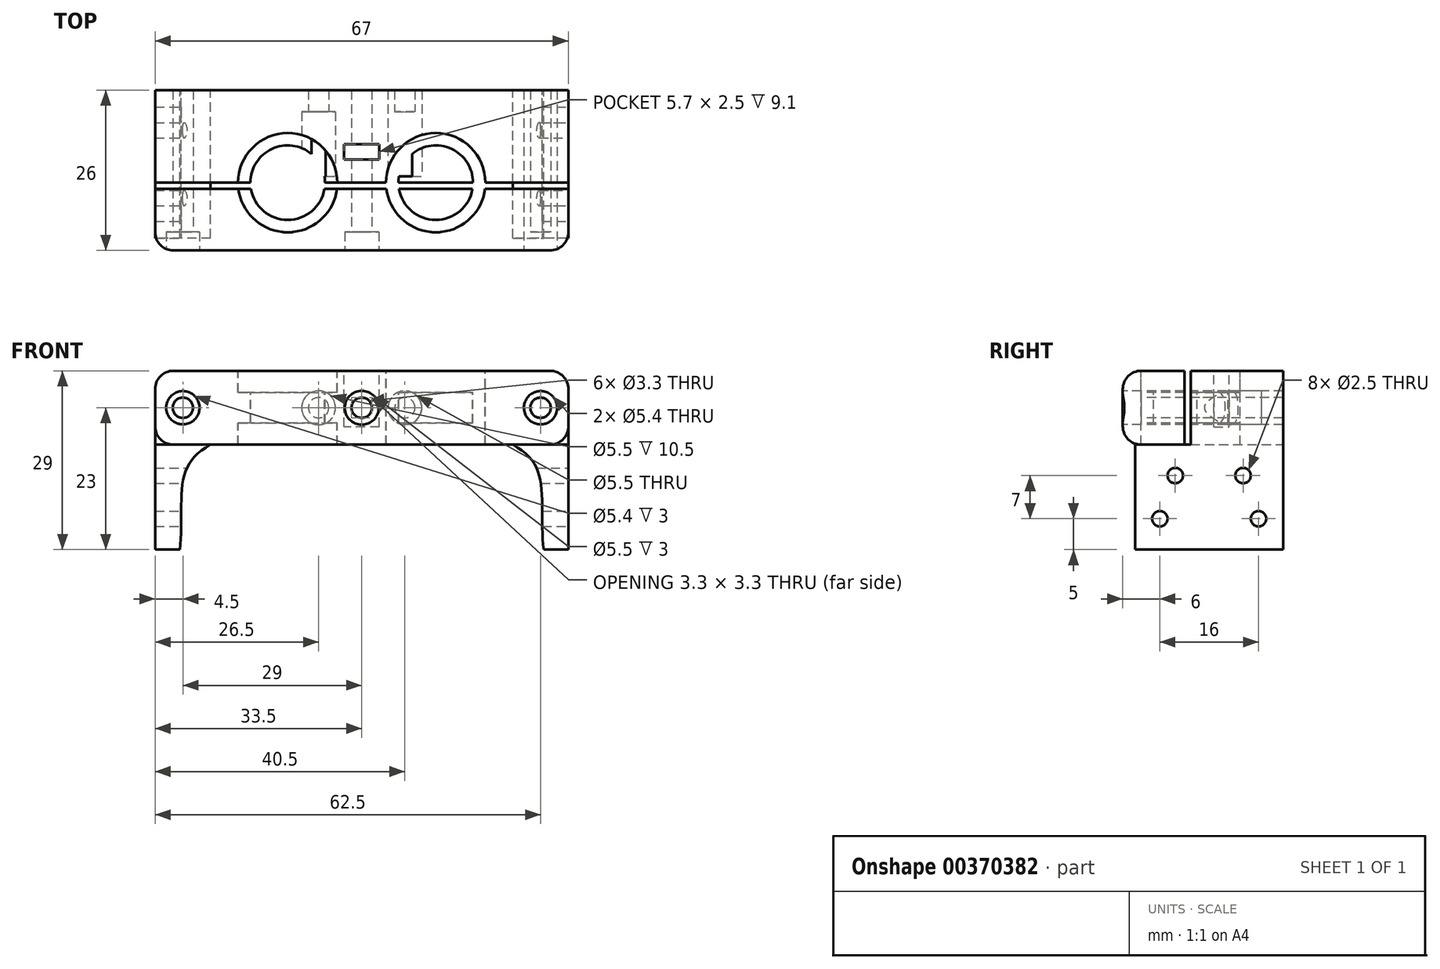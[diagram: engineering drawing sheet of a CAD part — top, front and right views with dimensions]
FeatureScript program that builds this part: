
annotation { "Feature Type Name" : "Feature", "Feature Type Description" : "" }
export const myFeature = defineFeature(function(context is Context, id is Id, definition is map)
    precondition{}
    {
        {
            var Q0;
            Q0=qCreatedBy(makeId("Front.planeOp"),FACE);
            var sketch = newSketch(context, id + "F0", { "sketchPlane" : qUnion([Q0])});
            skLineSegment(sketch, "E0.bottom", {"start": v(33.5, -6) * mm, "end": v(-33.5, -6) * mm});
            skLineSegment(sketch, "E0.top", {"start": v(33.5, 6) * mm, "end": v(-33.5, 6) * mm});
            skLineSegment(sketch, "E0.left", {"start": v(33.5, -6) * mm, "end": v(33.5, 6) * mm});
            skLineSegment(sketch, "E0.right", {"start": v(-33.5, -6) * mm, "end": v(-33.5, 6) * mm});
            skPoint(sketch, "E0.middle", {"position": v(0, 0) * mm});
            skLineSegment(sketch, "E1", {"start": v(-33.5, -23) * mm, "end": v(-33.5, -6) * mm});
            skLineSegment(sketch, "E2.MirrorCS", {"start": v(33.5, -23) * mm, "end": v(33.5, -6) * mm});
            skLineSegment(sketch, "E3", {"start": v(-33.5, -23) * mm, "end": v(-29.5, -23) * mm});
            skLineSegment(sketch, "E4.MirrorCS", {"start": v(33.5, -23) * mm, "end": v(29.5, -23) * mm});
            skFitSpline(sketch, "E5", {"points": [v(-24.5, -6) * mm, v(-29, -12) * mm, v(-29.5, -23) * mm], "startDerivative": vector(-19.18, -10.42) * mm, "endDerivative": vector(-2.52, -19.68) * mm});
            skFitSpline(sketch, "E6.MirrorCS", {"points": [v(24.5, -6) * mm, v(29, -12) * mm, v(29.5, -23) * mm], "startDerivative": vector(19.18, -10.42) * mm, "endDerivative": vector(2.52, -19.68) * mm});
            skSolve(sketch);
        }
        {
            var Q0;
            Q0=makeQuery(id+"F0.imprint","IMPRINT",FACE,{"disambiguationData":[TD([[makeQuery(id+"F0.imprint","IMPRINT",EDGE,{"derivedFrom":sQuery(id+"F0.wireOp",EDGE,"E0.top")}),1.0]])]});
            extrude(context, id + "F1", {"entities" : qUnion([Q0]), "depth" : 15 * mm, "offsetDistance" : 25 * mm});
        }
        {
            var Q0;
            {var subQ0=sQuery(id+"F0.wireOp",EDGE,"E1");Q0=makeQuery(id+"F0.imprint","IMPRINT",FACE,{"disambiguationData":[TD([[makeQuery(id+"F0.imprint","IMPRINT",EDGE,{"derivedFrom":subQ0}),-1.0]])]});}
            var Q1;
            {var subQ0=sQuery(id+"F0.wireOp",EDGE,"E2.MirrorCS");Q1=makeQuery(id+"F0.imprint","IMPRINT",FACE,{"disambiguationData":[TD([[makeQuery(id+"F0.imprint","IMPRINT",EDGE,{"derivedFrom":subQ0}),1.0]])]});}
            extrude(context, id + "F2", {"entities" : qUnion([Q0, Q1]), "operationType" : NewBodyOperationType.ADD, "depth" : 24 * mm, "offsetDistance" : 25 * mm});
        }
        {
            var Q0;
            Q0=makeQuery(id+"F1.opExtrude","SWEPT_FACE",FACE,{"disambiguationData":[OSD([sQuery(id+"F0.wireOp",EDGE,"E0.top")])]});
            var sketch = newSketch(context, id + "F3", { "sketchPlane" : qUnion([Q0])});
            skLineSegment(sketch, "E7", {"start": v(-33.5, -7) * mm, "end": v(33.5, -7) * mm, "construction": true});
            skLineSegment(sketch, "E8.bottom", {"start": v(2.85, -11.25) * mm, "end": v(-2.85, -11.25) * mm});
            skLineSegment(sketch, "E8.top", {"start": v(2.85, -8.75) * mm, "end": v(-2.85, -8.75) * mm});
            skLineSegment(sketch, "E8.left", {"start": v(2.85, -11.25) * mm, "end": v(2.85, -8.75) * mm});
            skLineSegment(sketch, "E8.right", {"start": v(-2.85, -11.25) * mm, "end": v(-2.85, -8.75) * mm});
            skPoint(sketch, "E8.middle", {"position": v(0, -10) * mm});
            skSolve(sketch);
        }
        {
            var Q0;
            Q0=makeQuery(id+"F3.imprint","IMPRINT",FACE,{"disambiguationData":[TD([[makeQuery(id+"F3.imprint","IMPRINT",EDGE,{"derivedFrom":sQuery(id+"F3.wireOp",EDGE,"jUf4XIvJ-XALh-Ccey-Qydy-tmJyOFJsBozL.bottom")}),-1.0]])]});
            var Q1;
            Q1=makeQuery(id+"F3.imprint","IMPRINT",FACE,{"disambiguationData":[TD([[makeQuery(id+"F3.imprint","IMPRINT",EDGE,{"derivedFrom":sQuery(id+"F3.wireOp",EDGE,"E8.bottom")}),-1.0]])]});
            var Q2;
            Q2=makeQuery(id+"F3.imprint","IMPRINT",FACE,{"disambiguationData":[TD([[makeQuery(id+"F3.imprint","IMPRINT",EDGE,{"derivedFrom":sQuery(id+"F3.wireOp",EDGE,"7975c7f9-c37b-4ea5-b004-56becf66a4950.MirrorCS")}),1.0]])]});
            extrude(context, id + "F4", {"entities" : qUnion([Q0, Q1, Q2]), "operationType" : NewBodyOperationType.REMOVE, "oppositeDirection" : true, "depth" : 9.1 * mm, "offsetDistance" : 25 * mm});
        }
        {
            var Q0;
            Q0=qCreatedBy(makeId("Top.planeOp"),FACE);
            var sketch = newSketch(context, id + "F5", { "sketchPlane" : qUnion([Q0])});
            skLineSegment(sketch, "E9.bottom", {"start": v(33.5, -26) * mm, "end": v(-33.5, -26) * mm});
            skLineSegment(sketch, "E9.top", {"start": v(33.5, -16) * mm, "end": v(-33.5, -16) * mm});
            skLineSegment(sketch, "E9.left", {"start": v(33.5, -26) * mm, "end": v(33.5, -16) * mm});
            skLineSegment(sketch, "E9.right", {"start": v(-33.5, -26) * mm, "end": v(-33.5, -16) * mm});
            skPoint(sketch, "E9.middle", {"position": v(0, -21) * mm});
            skSolve(sketch);
        }
        {
            var Q0;
            Q0=makeQuery(id+"F5.imprint","IMPRINT",FACE,{"disambiguationData":[TD([[makeQuery(id+"F5.imprint","IMPRINT",EDGE,{"derivedFrom":sQuery(id+"F5.wireOp",EDGE,"E9.bottom")}),-1.0]])]});
            extrude(context, id + "F6", {"entities" : qUnion([Q0]), "endBound" : BoundingType.SYMMETRIC, "depth" : 12 * mm, "offsetDistance" : 25 * mm});
        }
        {
            var Q0;
            Q0=makeQuery(id+"F6.opExtrude","SWEPT_FACE",FACE,{"disambiguationData":[OSD([sQuery(id+"F5.wireOp",EDGE,"E9.bottom")])]});
            var sketch = newSketch(context, id + "F7", { "sketchPlane" : qUnion([Q0])});
            skCircle(sketch, "E10", {"center": v(-7, 0) * mm, "radius": 1.65 * mm});
            skCircle(sketch, "E11.MirrorC", {"center": v(7, 0) * mm, "radius": 1.65 * mm});
            skCircle(sketch, "E12", {"center": v(-7, 0) * mm, "radius": 2.75 * mm});
            skCircle(sketch, "E13.MirrorC", {"center": v(7, 0) * mm, "radius": 2.75 * mm});
            skCircle(sketch, "E14", {"center": v(-29, 0) * mm, "radius": 1.65 * mm});
            skCircle(sketch, "E15", {"center": v(0, 0) * mm, "radius": 1.65 * mm});
            skCircle(sketch, "E16.MirrorC", {"center": v(29, 0) * mm, "radius": 1.65 * mm});
            skCircle(sketch, "E17", {"center": v(-29, 0) * mm, "radius": 2.7 * mm});
            skCircle(sketch, "E18", {"center": v(0, 0) * mm, "radius": 2.75 * mm});
            skCircle(sketch, "E19", {"center": v(29, 0) * mm, "radius": 2.7 * mm});
            skSolve(sketch);
        }
        {
            var Q0;
            Q0=makeQuery(id+"F7.imprint","IMPRINT",FACE,{"disambiguationData":[TD([[makeQuery(id+"F7.imprint","IMPRINT",EDGE,{"derivedFrom":sQuery(id+"F7.wireOp",EDGE,"E10")}),1.0]])]});
            var Q1;
            Q1=makeQuery(id+"F7.imprint","IMPRINT",FACE,{"disambiguationData":[TD([[makeQuery(id+"F7.imprint","IMPRINT",EDGE,{"derivedFrom":sQuery(id+"F7.wireOp",EDGE,"E11.MirrorC")}),-1.0]])]});
            extrude(context, id + "F8", {"entities" : qUnion([Q0, Q1]), "operationType" : NewBodyOperationType.REMOVE, "oppositeDirection" : true, "depth" : 30.5 * mm, "offsetDistance" : 25 * mm, "hasSecondDirection" : true, "secondDirectionOppositeDirection" : true, "secondDirectionDepth" : 12 * mm});
        }
        {
            var Q0;
            Q0=makeQuery(id+"F7.imprint","IMPRINT",FACE,{"disambiguationData":[TD([[makeQuery(id+"F7.imprint","IMPRINT",EDGE,{"derivedFrom":sQuery(id+"F7.wireOp",EDGE,"E10")}),-1.0]])]});
            var Q1;
            Q1=makeQuery(id+"F7.imprint","IMPRINT",FACE,{"disambiguationData":[TD([[makeQuery(id+"F7.imprint","IMPRINT",EDGE,{"derivedFrom":sQuery(id+"F7.wireOp",EDGE,"E11.MirrorC")}),1.0]])]});
            extrude(context, id + "F9", {"entities" : qUnion([Q0, Q1]), "operationType" : NewBodyOperationType.REMOVE, "oppositeDirection" : true, "depth" : 22.5 * mm, "offsetDistance" : 25 * mm, "hasSecondDirection" : true, "secondDirectionOppositeDirection" : true, "secondDirectionDepth" : 12 * mm});
        }
        {
            var Q0;
            Q0=makeQuery(id+"F7.imprint","IMPRINT",FACE,{"disambiguationData":[TD([[makeQuery(id+"F7.imprint","IMPRINT",EDGE,{"derivedFrom":sQuery(id+"F7.wireOp",EDGE,"E14")}),1.0]])]});
            var Q1;
            Q1=makeQuery(id+"F7.imprint","IMPRINT",FACE,{"disambiguationData":[TD([[makeQuery(id+"F7.imprint","IMPRINT",EDGE,{"derivedFrom":sQuery(id+"F7.wireOp",EDGE,"E15")}),1.0]])]});
            var Q2;
            Q2=makeQuery(id+"F7.imprint","IMPRINT",FACE,{"disambiguationData":[TD([[makeQuery(id+"F7.imprint","IMPRINT",EDGE,{"derivedFrom":sQuery(id+"F7.wireOp",EDGE,"E16.MirrorC")}),-1.0]])]});
            extrude(context, id + "F10", {"entities" : qUnion([Q0, Q1, Q2]), "operationType" : NewBodyOperationType.REMOVE, "oppositeDirection" : true, "depth" : 45 * mm, "offsetDistance" : 25 * mm});
        }
        {
            var Q0;
            Q0=makeQuery(id+"F1.opExtrude","SWEPT_FACE",FACE,{"disambiguationData":[OSD([sQuery(id+"F0.wireOp",EDGE,"E0.top")])]});
            var sketch = newSketch(context, id + "F11", { "sketchPlane" : qUnion([Q0])});
            skCircle(sketch, "E20", {"center": v(-12, -15) * mm, "radius": 8.05 * mm});
            skCircle(sketch, "E21", {"center": v(-12, -15) * mm, "radius": 6.05 * mm});
            skCircle(sketch, "E22.MirrorC", {"center": v(12, -15) * mm, "radius": 6.05 * mm});
            skCircle(sketch, "E23.MirrorC", {"center": v(12, -15) * mm, "radius": 8.05 * mm});
            skSolve(sketch);
        }
        {
            var Q0;
            {var subQ0=sQuery(id+"F11.wireOp",EDGE,"E21");var subQ1=makeQuery(id+"F1.opExtrude","CAP_EDGE",EDGE,{"disambiguationData":[OSD([sQuery(id+"F0.wireOp",EDGE,"E0.top")])],"isStart":false});var subQ2=makeQuery(id+"F11.imprint","INTERSECT",VERTEX,{"disambiguationData":[OD(0.0)],"derivedFrom":[subQ1,subQ0]});Q0=makeQuery(id+"F11.imprint","IMPRINT",FACE,{"disambiguationData":[TD([[makeQuery(id+"F11.imprint","IMPRINT",EDGE,{"disambiguationData":[TD([[subQ2,1.0]])],"derivedFrom":subQ0}),1.0]])]});}
            var Q1;
            {var subQ0=sQuery(id+"F11.wireOp",EDGE,"E22.MirrorC");var subQ1=makeQuery(id+"F1.opExtrude","CAP_EDGE",EDGE,{"disambiguationData":[OSD([sQuery(id+"F0.wireOp",EDGE,"E0.top")])],"isStart":false});var subQ2=makeQuery(id+"F11.imprint","INTERSECT",VERTEX,{"disambiguationData":[OD(0.0)],"derivedFrom":[subQ1,subQ0]});Q1=makeQuery(id+"F11.imprint","IMPRINT",FACE,{"disambiguationData":[TD([[makeQuery(id+"F11.imprint","IMPRINT",EDGE,{"disambiguationData":[TD([[subQ2,1.0]])],"derivedFrom":subQ0}),-1.0]])]});}
            var Q2;
            {var subQ0=sQuery(id+"F11.wireOp",EDGE,"E21");var subQ1=makeQuery(id+"F1.opExtrude","CAP_EDGE",EDGE,{"disambiguationData":[OSD([sQuery(id+"F0.wireOp",EDGE,"E0.top")])],"isStart":false});var subQ2=makeQuery(id+"F11.imprint","INTERSECT",VERTEX,{"disambiguationData":[OD(0.0)],"derivedFrom":[subQ1,subQ0]});Q2=makeQuery(id+"F11.imprint","IMPRINT",FACE,{"disambiguationData":[TD([[makeQuery(id+"F11.imprint","IMPRINT",EDGE,{"disambiguationData":[TD([[subQ2,-1.0]])],"derivedFrom":subQ0}),1.0]])]});}
            var Q3;
            {var subQ0=sQuery(id+"F11.wireOp",EDGE,"E22.MirrorC");var subQ1=makeQuery(id+"F1.opExtrude","CAP_EDGE",EDGE,{"disambiguationData":[OSD([sQuery(id+"F0.wireOp",EDGE,"E0.top")])],"isStart":false});var subQ2=makeQuery(id+"F11.imprint","INTERSECT",VERTEX,{"disambiguationData":[OD(0.0)],"derivedFrom":[subQ1,subQ0]});Q3=makeQuery(id+"F11.imprint","IMPRINT",FACE,{"disambiguationData":[TD([[makeQuery(id+"F11.imprint","IMPRINT",EDGE,{"disambiguationData":[TD([[subQ2,-1.0]])],"derivedFrom":subQ0}),-1.0]])]});}
            extrude(context, id + "F12", {"entities" : qUnion([Q0, Q1, Q2, Q3]), "operationType" : NewBodyOperationType.REMOVE, "endBound" : BoundingType.THROUGH_ALL, "oppositeDirection" : true, "depth" : 25 * mm, "offsetDistance" : 25 * mm});
        }
        {
            var Q0;
            {var subQ0=sQuery(id+"F11.wireOp",EDGE,"E20");var subQ1=makeQuery(id+"F1.opExtrude","CAP_EDGE",EDGE,{"disambiguationData":[OSD([sQuery(id+"F0.wireOp",EDGE,"E0.top")])],"isStart":false});var subQ2=makeQuery(id+"F11.imprint","INTERSECT",VERTEX,{"disambiguationData":[OD(0.0)],"derivedFrom":[subQ1,subQ0]});Q0=makeQuery(id+"F11.imprint","IMPRINT",FACE,{"disambiguationData":[TD([[makeQuery(id+"F11.imprint","IMPRINT",EDGE,{"disambiguationData":[TD([[subQ2,1.0]])],"derivedFrom":subQ0}),1.0]])]});}
            var Q1;
            {var subQ0=sQuery(id+"F11.wireOp",EDGE,"E22.MirrorC");var subQ1=makeQuery(id+"F1.opExtrude","CAP_EDGE",EDGE,{"disambiguationData":[OSD([sQuery(id+"F0.wireOp",EDGE,"E0.top")])],"isStart":false});var subQ2=makeQuery(id+"F11.imprint","INTERSECT",VERTEX,{"disambiguationData":[OD(0.0)],"derivedFrom":[subQ1,subQ0]});Q1=makeQuery(id+"F11.imprint","IMPRINT",FACE,{"disambiguationData":[TD([[makeQuery(id+"F11.imprint","IMPRINT",EDGE,{"disambiguationData":[TD([[subQ2,1.0]])],"derivedFrom":subQ0}),1.0]])]});}
            var Q2;
            {var subQ0=sQuery(id+"F11.wireOp",EDGE,"E20");var subQ1=makeQuery(id+"F1.opExtrude","CAP_EDGE",EDGE,{"disambiguationData":[OSD([sQuery(id+"F0.wireOp",EDGE,"E0.top")])],"isStart":false});var subQ2=makeQuery(id+"F11.imprint","INTERSECT",VERTEX,{"disambiguationData":[OD(0.0)],"derivedFrom":[subQ1,subQ0]});Q2=makeQuery(id+"F11.imprint","IMPRINT",FACE,{"disambiguationData":[TD([[makeQuery(id+"F11.imprint","IMPRINT",EDGE,{"disambiguationData":[TD([[subQ2,-1.0]])],"derivedFrom":subQ0}),1.0]])]});}
            var Q3;
            {var subQ0=sQuery(id+"F11.wireOp",EDGE,"E22.MirrorC");var subQ1=makeQuery(id+"F1.opExtrude","CAP_EDGE",EDGE,{"disambiguationData":[OSD([sQuery(id+"F0.wireOp",EDGE,"E0.top")])],"isStart":false});var subQ2=makeQuery(id+"F11.imprint","INTERSECT",VERTEX,{"disambiguationData":[OD(0.0)],"derivedFrom":[subQ1,subQ0]});Q3=makeQuery(id+"F11.imprint","IMPRINT",FACE,{"disambiguationData":[TD([[makeQuery(id+"F11.imprint","IMPRINT",EDGE,{"disambiguationData":[TD([[subQ2,-1.0]])],"derivedFrom":subQ0}),1.0]])]});}
            extrude(context, id + "F13", {"entities" : qUnion([Q0, Q1, Q2, Q3]), "operationType" : NewBodyOperationType.REMOVE, "oppositeDirection" : true, "depth" : 3.5 * mm, "offsetDistance" : 25 * mm});
        }
        {
            var Q0;
            {var subQ0=sQuery(id+"F11.wireOp",EDGE,"E20");var subQ1=makeQuery(id+"F1.opExtrude","CAP_EDGE",EDGE,{"disambiguationData":[OSD([sQuery(id+"F0.wireOp",EDGE,"E0.top")])],"isStart":false});var subQ2=makeQuery(id+"F11.imprint","INTERSECT",VERTEX,{"disambiguationData":[OD(0.0)],"derivedFrom":[subQ1,subQ0]});Q0=makeQuery(id+"F11.imprint","IMPRINT",FACE,{"disambiguationData":[TD([[makeQuery(id+"F11.imprint","IMPRINT",EDGE,{"disambiguationData":[TD([[subQ2,1.0]])],"derivedFrom":subQ0}),1.0]])]});}
            var Q1;
            {var subQ0=sQuery(id+"F11.wireOp",EDGE,"E22.MirrorC");var subQ1=makeQuery(id+"F1.opExtrude","CAP_EDGE",EDGE,{"disambiguationData":[OSD([sQuery(id+"F0.wireOp",EDGE,"E0.top")])],"isStart":false});var subQ2=makeQuery(id+"F11.imprint","INTERSECT",VERTEX,{"disambiguationData":[OD(0.0)],"derivedFrom":[subQ1,subQ0]});Q1=makeQuery(id+"F11.imprint","IMPRINT",FACE,{"disambiguationData":[TD([[makeQuery(id+"F11.imprint","IMPRINT",EDGE,{"disambiguationData":[TD([[subQ2,1.0]])],"derivedFrom":subQ0}),1.0]])]});}
            var Q2;
            {var subQ0=sQuery(id+"F11.wireOp",EDGE,"E20");var subQ1=makeQuery(id+"F1.opExtrude","CAP_EDGE",EDGE,{"disambiguationData":[OSD([sQuery(id+"F0.wireOp",EDGE,"E0.top")])],"isStart":false});var subQ2=makeQuery(id+"F11.imprint","INTERSECT",VERTEX,{"disambiguationData":[OD(0.0)],"derivedFrom":[subQ1,subQ0]});Q2=makeQuery(id+"F11.imprint","IMPRINT",FACE,{"disambiguationData":[TD([[makeQuery(id+"F11.imprint","IMPRINT",EDGE,{"disambiguationData":[TD([[subQ2,-1.0]])],"derivedFrom":subQ0}),1.0]])]});}
            var Q3;
            {var subQ0=sQuery(id+"F11.wireOp",EDGE,"E22.MirrorC");var subQ1=makeQuery(id+"F1.opExtrude","CAP_EDGE",EDGE,{"disambiguationData":[OSD([sQuery(id+"F0.wireOp",EDGE,"E0.top")])],"isStart":false});var subQ2=makeQuery(id+"F11.imprint","INTERSECT",VERTEX,{"disambiguationData":[OD(0.0)],"derivedFrom":[subQ1,subQ0]});Q3=makeQuery(id+"F11.imprint","IMPRINT",FACE,{"disambiguationData":[TD([[makeQuery(id+"F11.imprint","IMPRINT",EDGE,{"disambiguationData":[TD([[subQ2,-1.0]])],"derivedFrom":subQ0}),1.0]])]});}
            extrude(context, id + "F14", {"entities" : qUnion([Q0, Q1, Q2, Q3]), "operationType" : NewBodyOperationType.REMOVE, "oppositeDirection" : true, "depth" : 12 * mm, "offsetDistance" : 25 * mm, "hasSecondDirection" : true, "secondDirectionOppositeDirection" : true, "secondDirectionDepth" : 8.5 * mm});
        }
        {
            var Q0;
            Q0=makeQuery(id+"F7.imprint","IMPRINT",FACE,{"disambiguationData":[TD([[makeQuery(id+"F7.imprint","IMPRINT",EDGE,{"derivedFrom":sQuery(id+"F7.wireOp",EDGE,"E14")}),-1.0]])]});
            var Q1;
            Q1=makeQuery(id+"F7.imprint","IMPRINT",FACE,{"disambiguationData":[TD([[makeQuery(id+"F7.imprint","IMPRINT",EDGE,{"derivedFrom":sQuery(id+"F7.wireOp",EDGE,"E16.MirrorC")}),1.0]])]});
            var Q2;
            Q2=makeQuery(id+"F7.imprint","IMPRINT",FACE,{"disambiguationData":[TD([[makeQuery(id+"F7.imprint","IMPRINT",EDGE,{"derivedFrom":sQuery(id+"F7.wireOp",EDGE,"E15")}),-1.0]])]});
            extrude(context, id + "F15", {"entities" : qUnion([Q0, Q1, Q2]), "operationType" : NewBodyOperationType.REMOVE, "oppositeDirection" : true, "depth" : 3 * mm, "offsetDistance" : 25 * mm});
        }
        {
            var Q0;
            Q0=makeQuery(id+"F1.opExtrude","SWEPT_EDGE",EDGE,{"disambiguationData":[OSD([sQuery(id+"F0.wireOp",EDGE,"E0.top"),sQuery(id+"F0.wireOp",EDGE,"E0.left")])]});
            var Q1;
            Q1=makeQuery(id+"F6.opExtrude","SWEPT_EDGE",EDGE,{"disambiguationData":[OSD([sQuery(id+"F5.wireOp",EDGE,"E9.bottom"),sQuery(id+"F5.wireOp",EDGE,"E9.right")])]});
            var Q2;
            Q2=makeQuery(id+"F6.opExtrude","SWEPT_EDGE",EDGE,{"disambiguationData":[OSD([sQuery(id+"F5.wireOp",EDGE,"E9.bottom"),sQuery(id+"F5.wireOp",EDGE,"E9.left")])]});
            var Q3;
            Q3=makeQuery(id+"F6.opExtrude","CAP_EDGE",EDGE,{"disambiguationData":[OSD([sQuery(id+"F5.wireOp",EDGE,"E9.bottom")])],"isStart":false});
            var Q4;
            Q4=makeQuery(id+"F6.opExtrude","CAP_EDGE",EDGE,{"disambiguationData":[OSD([sQuery(id+"F5.wireOp",EDGE,"E9.right")])],"isStart":false});
            var Q5;
            Q5=makeQuery(id+"F6.opExtrude","CAP_EDGE",EDGE,{"disambiguationData":[OSD([sQuery(id+"F5.wireOp",EDGE,"E9.left")])],"isStart":true});
            var Q6;
            Q6=makeQuery(id+"F6.opExtrude","CAP_EDGE",EDGE,{"disambiguationData":[OSD([sQuery(id+"F5.wireOp",EDGE,"E9.left")])],"isStart":false});
            var Q7;
            Q7=makeQuery(id+"F6.opExtrude","CAP_EDGE",EDGE,{"disambiguationData":[OSD([sQuery(id+"F5.wireOp",EDGE,"E9.right")])],"isStart":true});
            var Q8;
            Q8=makeQuery(id+"F6.opExtrude","CAP_EDGE",EDGE,{"disambiguationData":[OSD([sQuery(id+"F5.wireOp",EDGE,"E9.bottom")])],"isStart":true});
            var Q9;
            Q9=makeQuery(id+"F1.opExtrude","SWEPT_EDGE",EDGE,{"disambiguationData":[OSD([sQuery(id+"F0.wireOp",EDGE,"E0.top"),sQuery(id+"F0.wireOp",EDGE,"E0.right")])]});
            var Q10;
            Q10=makeQuery(id+"F1.opExtrude","SWEPT_EDGE",EDGE,{"disambiguationData":[OSD([sQuery(id+"F0.wireOp",EDGE,"E2.MirrorCS"),sQuery(id+"F0.wireOp",EDGE,"E4.MirrorCS")])]});
            var Q11;
            Q11=makeQuery(id+"F1.opExtrude","SWEPT_EDGE",EDGE,{"disambiguationData":[OSD([sQuery(id+"F0.wireOp",EDGE,"E1"),sQuery(id+"F0.wireOp",EDGE,"E3")])]});
            fillet(context, id + "F16", {"entities" : qUnion([Q0, Q1, Q2, Q3, Q4, Q5, Q6, Q7, Q8, Q9, Q10, Q11]), "radius" : 3 * mm, "tangentPropagation" : true, "allowEdgeOverflow" : false});
        }
        {
            var Q0;
            Q0=makeQuery(id+"F2.boolean.opBoolean","MERGE",FACE,{"derivedFrom":[makeQuery(id+"F1.opExtrude","SWEPT_FACE",FACE,{"disambiguationData":[OSD([sQuery(id+"F0.wireOp",EDGE,"E0.left")])]}),makeQuery(id+"F2.opExtrude","SWEPT_FACE",FACE,{"disambiguationData":[OSD([sQuery(id+"F0.wireOp",EDGE,"E2.MirrorCS")])]})]});
            var sketch = newSketch(context, id + "F17", { "sketchPlane" : qUnion([Q0])});
            skLineSegment(sketch, "E24", {"start": v(-24, -14.5) * mm, "end": v(0, -14.5) * mm, "construction": true});
            skLineSegment(sketch, "E25", {"start": v(-12, -23) * mm, "end": v(-12, 3) * mm, "construction": true});
            skCircle(sketch, "E26", {"center": v(-17.5, -11) * mm, "radius": 1.25 * mm});
            skCircle(sketch, "E27.MirrorC", {"center": v(-6.5, -11) * mm, "radius": 1.25 * mm});
            skCircle(sketch, "E28", {"center": v(-20, -18) * mm, "radius": 1.25 * mm});
            skCircle(sketch, "E29.MirrorC", {"center": v(-4, -18) * mm, "radius": 1.25 * mm});
            skSolve(sketch);
        }
        {
            var Q0;
            Q0 = qSketchRegion(id + "F17", true);
            extrude(context, id + "F18", {"entities" : qUnion([Q0]), "operationType" : NewBodyOperationType.REMOVE, "oppositeDirection" : true, "depth" : 100 * mm, "offsetDistance" : 25 * mm});
        }
    });
